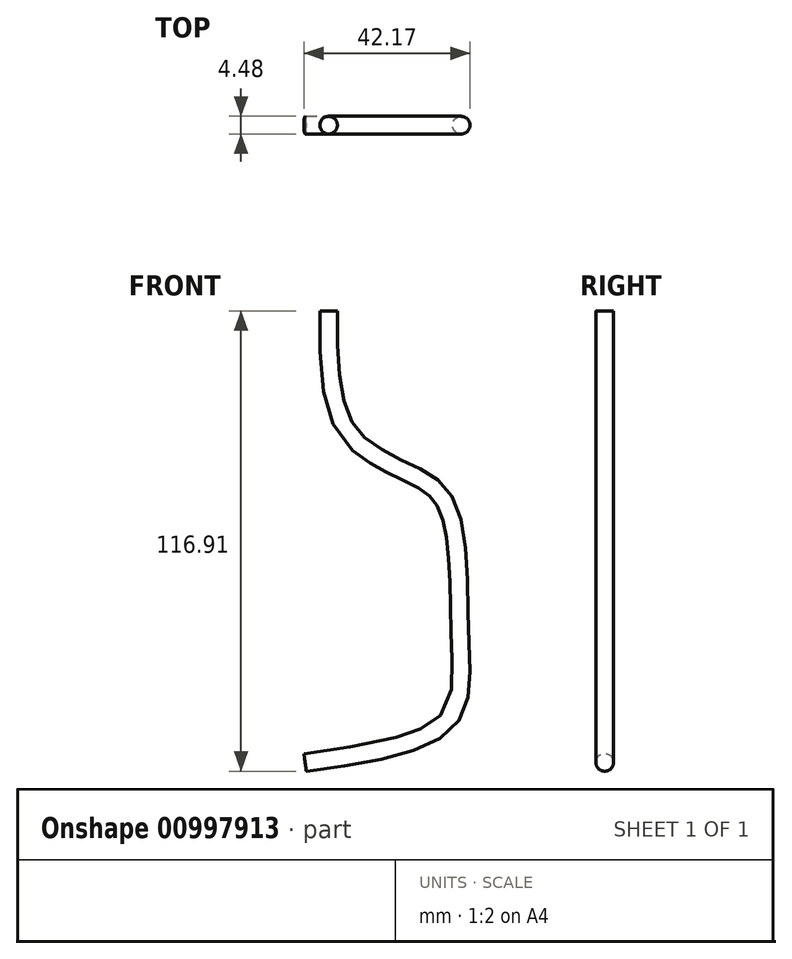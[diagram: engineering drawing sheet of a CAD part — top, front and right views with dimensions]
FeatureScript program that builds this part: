
annotation { "Feature Type Name" : "Feature", "Feature Type Description" : "" }
export const myFeature = defineFeature(function(context is Context, id is Id, definition is map)
    precondition{}
    {
        {
            var Q0;
            Q0=qCreatedBy(makeId("Front.planeOp"),FACE);
            var sketch = newSketch(context, id + "F0", { "sketchPlane" : qUnion([Q0])});
            skFitSpline(sketch, "E0", {"points": [v(6.24, 58.81) * mm, v(10.87, 28.6) * mm, v(25.98, 18.11) * mm, v(36.46, 9.17) * mm, v(39.54, -23.2) * mm, v(36.46, -45.4) * mm, v(0, -56.2) * mm], "startDerivative": vector(0, -206.69) * mm, "endDerivative": vector(-224.65, -30.73) * mm});
            skSolve(sketch);
        }
        {
            var Q0;
            Q0=qCreatedBy(makeId("Top.planeOp"),FACE);
            cPlane(context, id + "F1", {"entities" : qUnion([Q0]), "cplaneType" : CPlaneType.OFFSET, "offset" : 58.67 * mm, "width" : 152.4 * mm, "height" : 152.4 * mm});
        }
        {
            var Q0;
            Q0=qCreatedBy(id+"F1.planeOp",FACE);
            var sketch = newSketch(context, id + "F2", { "sketchPlane" : qUnion([Q0])});
            skCircle(sketch, "E1", {"center": v(5.94, 0) * mm, "radius": 2.24 * mm});
            skSolve(sketch);
        }
        {
            var Q0;
            Q0=makeQuery(id+"F2.imprint","IMPRINT",FACE,{"disambiguationData":[TD([[makeQuery(id+"F2.imprint","IMPRINT",EDGE,{"derivedFrom":sQuery(id+"F2.wireOp",EDGE,"E1")}),1.0]])]});
            var Q1;
            Q1=sQuery(id+"F0.wireOp",EDGE,"E0");
            sweep(context, id + "F3", {"profiles" : qUnion([Q0]), "path" : qUnion([Q1])});
        }
    });
